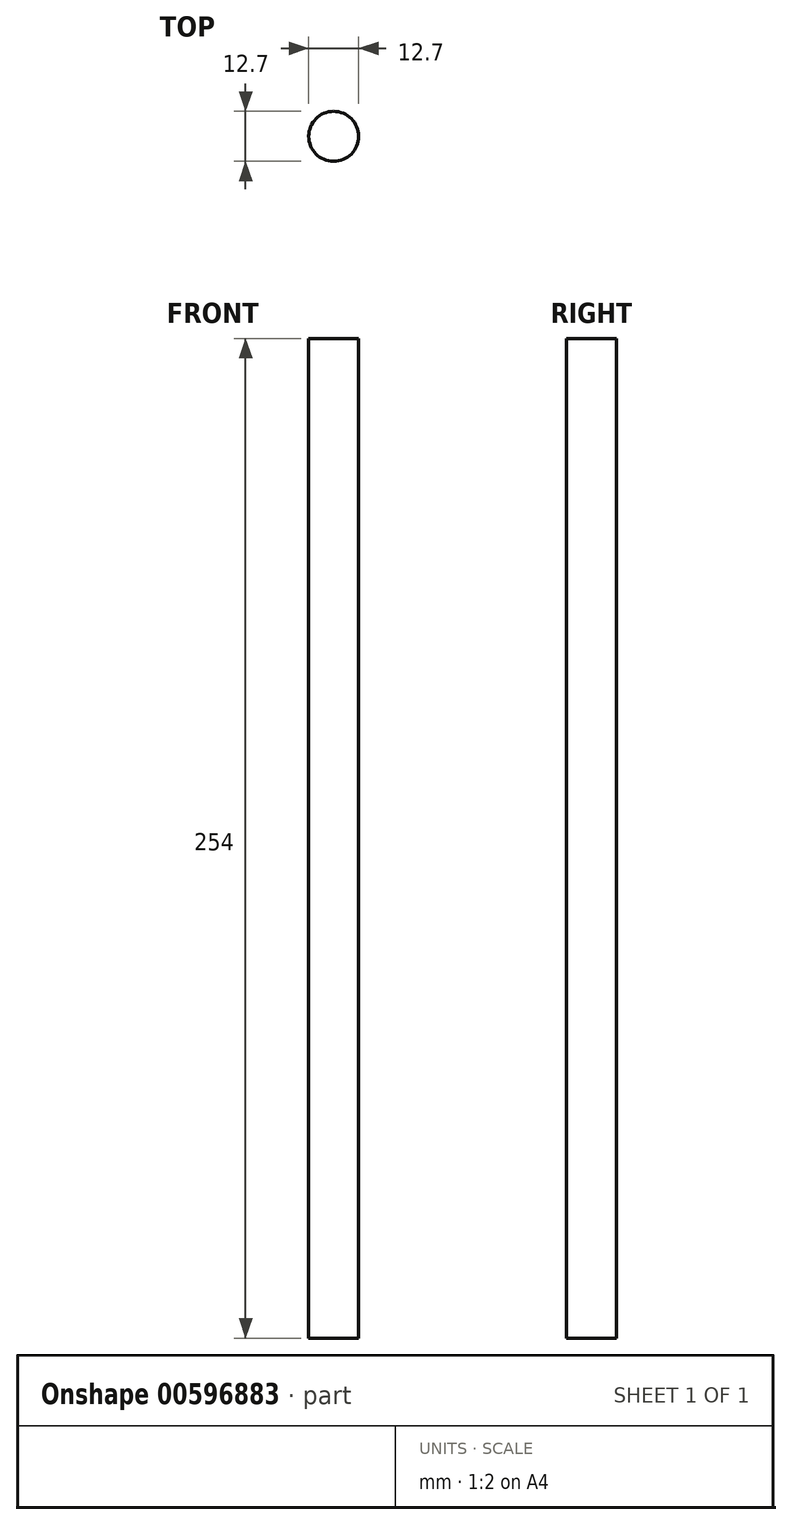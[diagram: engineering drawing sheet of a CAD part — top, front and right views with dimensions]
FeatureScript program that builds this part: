
annotation { "Feature Type Name" : "Feature", "Feature Type Description" : "" }
export const myFeature = defineFeature(function(context is Context, id is Id, definition is map)
    precondition{}
    {
        {
            var Q0;
            Q0=qCreatedBy(makeId("Top.planeOp"),FACE);
            var sketch = newSketch(context, id + "F0", { "sketchPlane" : qUnion([Q0])});
            skCircle(sketch, "E0", {"center": v(0, 0) * mm, "radius": 6.35 * mm});
            skSolve(sketch);
        }
        {
            var Q0;
            Q0 = qSketchRegion(id + "F0", true);
            extrude(context, id + "F1", {"entities" : qUnion([Q0]), "depth" : 254 * mm, "offsetDistance" : 25.4 * mm});
        }
    });
